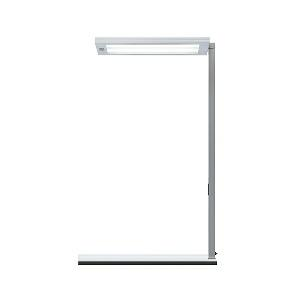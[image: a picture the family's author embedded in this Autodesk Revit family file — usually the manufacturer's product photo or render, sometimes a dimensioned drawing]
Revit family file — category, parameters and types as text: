
# Revit family: lavigo_-_dpt_14000_vtl_r_g2_00804513_3654
name_source: partatom
category: Lighting Fixtures
units: mm (PartAtom-declared; Revit-internal decimal feet)

## family parameters
Cut with Voids When Loaded = No
Host = Face
Light Source = No
Part Type = Normal
Room Calculation Point = No
Round Connector Dimension = Use Diameter
Shared = No

## types (1)
- LAVIGO - DPT 14000/VTL/R/G2 (1 x LED VTL, 14250 lm, 3000-6500K)
    Apparent Load = 100 VA
    Approval mark = CE
    CIE Flux Codes = 60 87 97 12 100
    Color Rendering = 80-89
    Color Temperature = 3000-6500K
    Control Gear = Electronic ballast
    Default Elevation = 1800 mm
    Description = DPT 14000/VTL/R/G2|Desk-mounted luminaire|light source: LED|work equipment: Electronic ballast|connected load: 220-240 V, 50/60 Hz|Power consumption: approx. 100 W|standby: approx. 0,50|power factor: approx. 0,965|luminous flux: 14250 lm|luminous efficacy: 142 lm/W|light distribution: Direct/indirect|direct ratio: approx. 12 %|colour temperature: , ca. 2700-6500 K|color rendering index (CRI): >= 80|technology: Presence and daylight sensor control (PIR)|operation: Multi-function switch|luminaire body|material: Steel/plastic|surface: Painted|colour: Silver metallic|lamp cover: Acrylic (PMMA), Satine|tubular section|material: Steel tube|surface: Painted|Form: Tubular section upright|colour of tubular section: Silver metallic|weight (net): approx. 15.4 kg|mains lead: 3.70 m Mains plug CEE 7/VII|Fastening: Socket, Table adaptor|decorative contrast side parts: Flint grey|glare control: Prism aperture|luminance(L65): <= 3000 cd/m|unified glare rating(4H 8H): <=  16|special features: Luminaire head detachable, Cradle to Cradle Certified TM, Direct light component with edge light and light-guide technology for homogenous light exit, Flicker-free, Indirect light component biodynamic light VTL, direct light component neutral working light, Integrated light and presence sensor PIR, Integrated light management for biodynamic light VTL, Retrofittable with TALK module, Inclination of tubular section adjustable, Separated, direct and indirect light individually adjustable|
    Frequency = 50 Hz, 60 Hz
    Height = 36 mm
    Lamp = 1 x LED VTL
    Lamp Light Flux = 14250 lm
    Lamp count = 1
    Length = 675 mm
    Luminous efficacy = 143 lm/W
    Manufacturer = Waldmann
    ModVariant = No
    Model = 00804513
    Mounting Place = Table
    Mounting Type = Surface mounted
    Number of Poles = 1
    OnlyDefault = Yes
    Power Factor = 1
    Product Name = LAVIGO - DPT 14000/VTL/R/G2
    Product group = Desk mounted luminaire with detector
    ProductGroupID = 2201
    Protection Class = Protection class I
    Protection Degree = IP 20
    RLX_Detail_Level = 1
    RLX_Emergency_Light_Flux = 0 lm
    RLX_Emergency_Type = 0
    RLX_Emergency_Type_DB = No
    RlxData = <blob elided: 35325 chars, md5=a3416944>
    Socket = socket
    Standby Power = 0 W
    System Light Flux = 14250 lm
    System Power = 100 W
    Type Comments = Product without accessories
    Type Image = 121716000-00666945.jpg
    URL = http://relux.com
    VarID = ---
    Voltage = 230 V
    Voltage Range = 220-240 V
    Weight = 0.00 kg
    Width = 320 mm

## geometry (parser evidence)
native form markers: Blend x4, Sweep x14
no freeform markers — native parametric forms only
